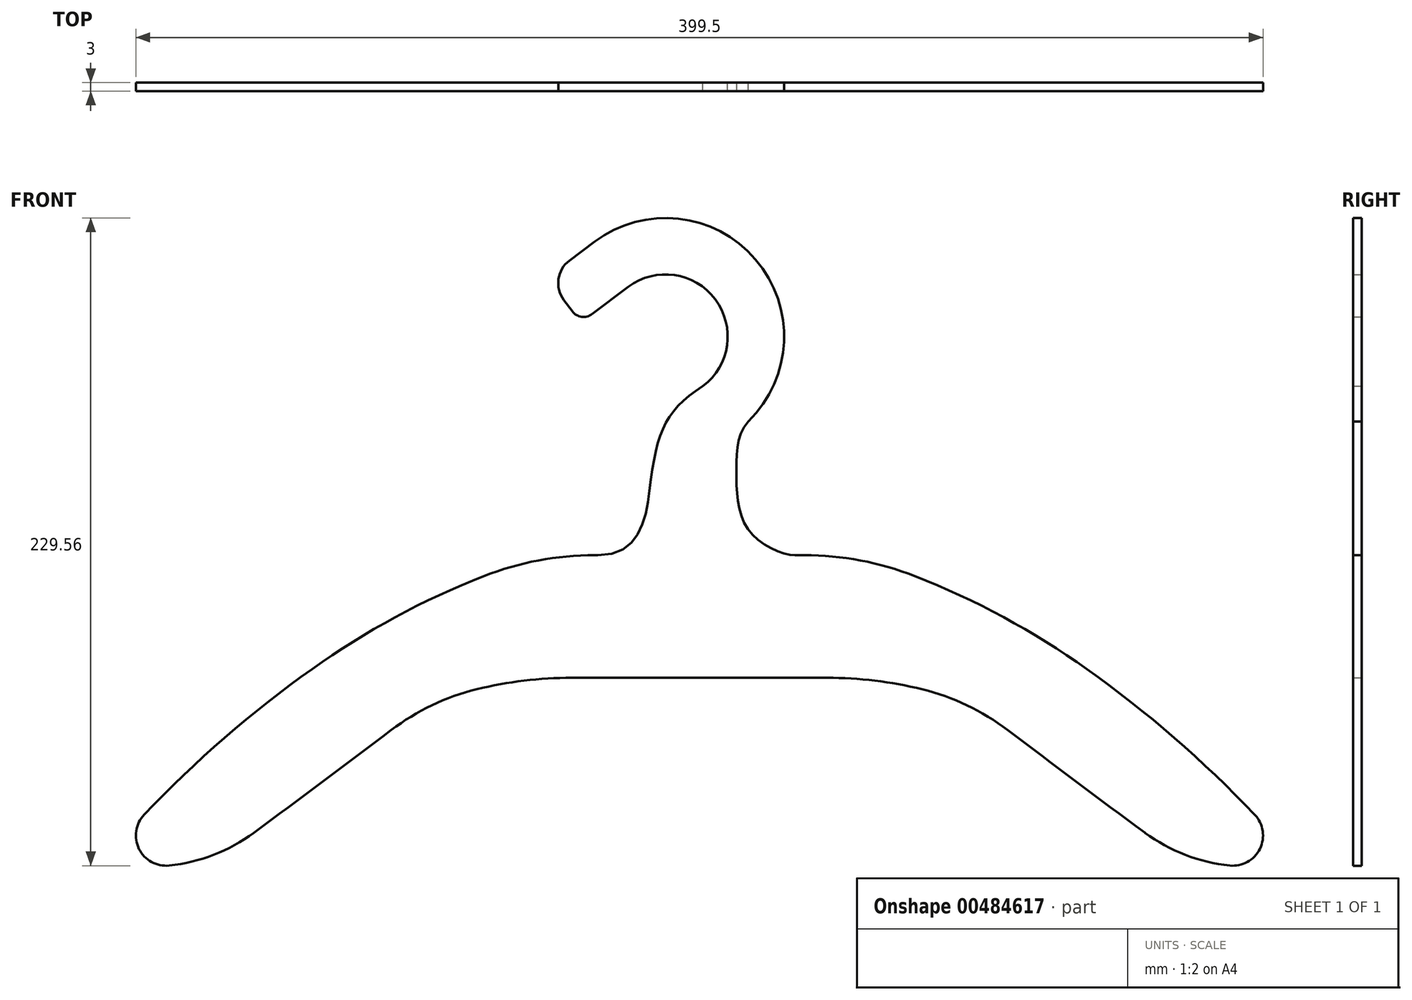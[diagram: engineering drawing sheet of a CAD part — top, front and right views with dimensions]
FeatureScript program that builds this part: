
annotation { "Feature Type Name" : "Feature", "Feature Type Description" : "" }
export const myFeature = defineFeature(function(context is Context, id is Id, definition is map)
    precondition{}
    {
        {
            var Q0;
            Q0=qCreatedBy(makeId("Front.planeOp"),FACE);
            var sketch = newSketch(context, id + "F0", { "sketchPlane" : qUnion([Q0])});
            skLineSegment(sketch, "E0", {"start": v(-37.13, 110) * mm, "end": v(0, 110) * mm});
            skArc(sketch, "E1", {"start": v(-37.13, 110) * mm, "mid": v(-57.05, 108.14) * mm, "end": v(-76.3, 102.62) * mm});
            skArc(sketch, "E2", {"start": v(-76.3, 102.62) * mm, "mid": v(-107.8, 88.02) * mm, "end": v(-137.29, 69.66) * mm});
            skArc(sketch, "E3", {"start": v(-137.29, 69.66) * mm, "mid": v(-168.3, 45.27) * mm, "end": v(-196.81, 18.01) * mm});
            skArc(sketch, "E4", {"start": v(-196.81, 18.01) * mm, "mid": v(-198.66, 5.92) * mm, "end": v(-187.96, 0) * mm});
            skArc(sketch, "E5", {"start": v(-187.96, 0) * mm, "mid": v(-172.17, 3.8) * mm, "end": v(-157.95, 11.62) * mm});
            skArc(sketch, "E6", {"start": v(-157.95, 11.62) * mm, "mid": v(-133.55, 29.75) * mm, "end": v(-109.25, 48.02) * mm});
            skArc(sketch, "E7", {"start": v(-109.25, 48.02) * mm, "mid": v(-94.82, 56.8) * mm, "end": v(-78.91, 62.47) * mm});
            skArc(sketch, "E8", {"start": v(-78.91, 62.47) * mm, "mid": v(-62.2, 65.53) * mm, "end": v(-45.23, 66.56) * mm});
            skLineSegment(sketch, "E9", {"start": v(0, 66.56) * mm, "end": v(-45.23, 66.56) * mm});
            skLineSegment(sketch, "E10.MirrorCS", {"start": v(37.13, 110) * mm, "end": v(0, 110) * mm});
            skArc(sketch, "E11.MirrorCS", {"start": v(37.13, 110) * mm, "mid": v(57.05, 108.14) * mm, "end": v(76.3, 102.62) * mm});
            skArc(sketch, "E12.MirrorCS", {"start": v(76.3, 102.62) * mm, "mid": v(107.8, 88.02) * mm, "end": v(137.29, 69.66) * mm});
            skArc(sketch, "E13.MirrorCS", {"start": v(137.29, 69.66) * mm, "mid": v(168.3, 45.27) * mm, "end": v(196.81, 18.01) * mm});
            skArc(sketch, "E14.MirrorCS", {"start": v(196.81, 18.01) * mm, "mid": v(198.66, 5.92) * mm, "end": v(187.96, 0) * mm});
            skArc(sketch, "E15.MirrorCS", {"start": v(187.96, 0) * mm, "mid": v(172.17, 3.8) * mm, "end": v(157.95, 11.62) * mm});
            skArc(sketch, "E16.MirrorCS", {"start": v(157.95, 11.62) * mm, "mid": v(133.55, 29.75) * mm, "end": v(109.25, 48.02) * mm});
            skArc(sketch, "E17.MirrorCS", {"start": v(109.25, 48.02) * mm, "mid": v(94.82, 56.8) * mm, "end": v(78.91, 62.47) * mm});
            skArc(sketch, "E18.MirrorCS", {"start": v(78.91, 62.47) * mm, "mid": v(62.2, 65.53) * mm, "end": v(45.23, 66.56) * mm});
            skLineSegment(sketch, "E19.MirrorCS", {"start": v(0, 66.56) * mm, "end": v(45.23, 66.56) * mm});
            skSolve(sketch);
        }
        {
            var Q0;
            Q0=qCreatedBy(makeId("Front.planeOp"),FACE);
            var sketch = newSketch(context, id + "F1", { "sketchPlane" : qUnion([Q0])});
            skPoint(sketch, "E20.0", {"position": v(0, 110) * mm});
            skLineSegment(sketch, "E21", {"start": v(0, 110) * mm, "end": v(0, 151.5) * mm});
            skArc(sketch, "E22", {"start": v(6, 163.5) * mm, "mid": v(12, 205.5) * mm, "end": v(-30, 211.5) * mm});
            skLineSegment(sketch, "E23", {"start": v(-30, 211.5) * mm, "end": v(-41.2, 203.1) * mm});
            skPoint(sketch, "E24.visualSharp", {"position": v(0, 160) * mm});
            skArc(sketch, "E24.filletArc", {"start": v(6, 163.5) * mm, "mid": v(1.58, 158.2) * mm, "end": v(0, 151.5) * mm});
            skLineSegment(sketch, "E25.0", {"start": v(-37.2, 221.1) * mm, "end": v(-46.06, 214.45) * mm});
            skArc(sketch, "E25.1", {"start": v(13.2, 153.9) * mm, "mid": v(21.6, 212.7) * mm, "end": v(-37.2, 221.1) * mm});
            skArc(sketch, "E25.2", {"start": v(13.2, 153.9) * mm, "mid": v(12.32, 152.84) * mm, "end": v(12, 151.5) * mm});
            skLineSegment(sketch, "E25.3", {"start": v(12, 110) * mm, "end": v(12, 151.5) * mm});
            skLineSegment(sketch, "E26.0", {"start": v(-25.2, 205.1) * mm, "end": v(-38.06, 195.45) * mm});
            skArc(sketch, "E26.1", {"start": v(1.2, 169.9) * mm, "mid": v(5.6, 200.7) * mm, "end": v(-25.2, 205.1) * mm});
            skArc(sketch, "E26.2", {"start": v(1.2, 169.9) * mm, "mid": v(-5.57, 161.78) * mm, "end": v(-8, 151.5) * mm});
            skLineSegment(sketch, "E26.3", {"start": v(-8, 110) * mm, "end": v(-8, 151.5) * mm});
            skLineSegment(sketch, "E27", {"start": v(-45.06, 196.45) * mm, "end": v(-48.06, 200.45) * mm});
            skPoint(sketch, "E28.visualSharp", {"position": v(-42.06, 192.45) * mm});
            skArc(sketch, "E28.filletArc", {"start": v(-45.06, 196.45) * mm, "mid": v(-41.77, 194.5) * mm, "end": v(-38.06, 195.45) * mm});
            skPoint(sketch, "E29.visualSharp", {"position": v(-54.06, 208.45) * mm});
            skArc(sketch, "E29.filletArc", {"start": v(-46.06, 214.45) * mm, "mid": v(-49.96, 207.87) * mm, "end": v(-48.06, 200.45) * mm});
            skLineSegment(sketch, "E30.0", {"start": v(37.13, 110) * mm, "end": v(0, 110) * mm});
            skLineSegment(sketch, "E30.1", {"start": v(-37.13, 110) * mm, "end": v(0, 110) * mm});
            skFitSpline(sketch, "E31", {"points": [v(-36.06, 110) * mm, v(-17.2, 136.96) * mm, v(-11.34, 157.85) * mm, v(1.2, 169.9) * mm], "startDerivative": vector(126.71, 0) * mm, "endDerivative": vector(61.94, 38.12) * mm});
            skFitSpline(sketch, "E32", {"points": [v(18.83, 158.98) * mm, v(13.1, 140.12) * mm, v(17.87, 118.31) * mm, v(33.81, 110) * mm], "startDerivative": vector(-51.04, -46.04) * mm, "endDerivative": vector(38.23, 0) * mm});
            skSolve(sketch);
        }
        {
            var Q0;
            Q0=qSketchRegion(id+"F0",true);
            extrude(context, id + "F2", {"entities" : qUnion([Q0]), "depth" : 3 * mm, "offsetDistance" : 25 * mm});
        }
        {
            var Q0;
            Q0=qSketchRegion(id+"F1",true);
            extrude(context, id + "F3", {"entities" : qUnion([Q0]), "operationType" : NewBodyOperationType.ADD, "depth" : 3 * mm, "offsetDistance" : 25 * mm});
        }
    });
